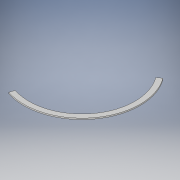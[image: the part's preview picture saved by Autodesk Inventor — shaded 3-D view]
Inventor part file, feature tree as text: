
AUTODESK INVENTOR PART (.ipt)
format: ipt  version: 2017 (Build 210142000, 142)  size: 106,496 bytes
history: native  units: in
note: dims shown in document units (in); Inventor stores cm internally (conversion verified against a paired STEP export)
features: extrude x1, sketch x1
ambient origin geometry x8: Origin, YZ Plane, XZ Plane, XY Plane, X Axis, Y Axis, Z Axis, Center Point
bodies: Solid1 (feature_tree)
feature tree (2):
  extrude  "Extrusion1"  Depth=0.125in TaperAngle=0.0deg
  sketch  "Sketch1"  dims[d0=5.2in d1=5.2in d2=5.2in d3=5.2in d4=5.2in d5=11.4in d6=0.4947in d7=0.125in d8=0.0in]
